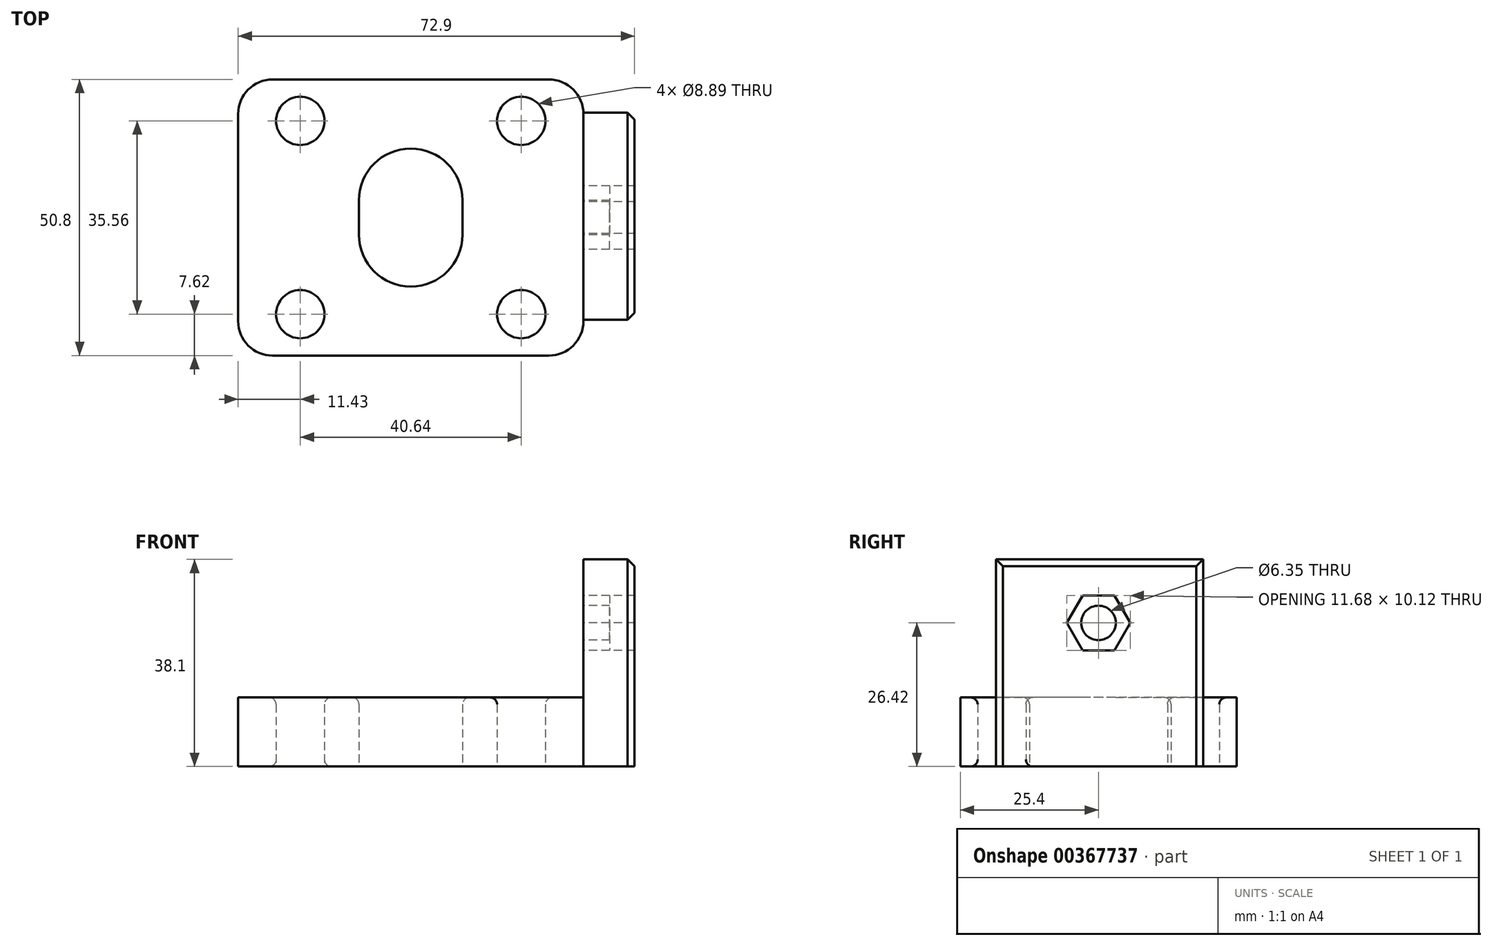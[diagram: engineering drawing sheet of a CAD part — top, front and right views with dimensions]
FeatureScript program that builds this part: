
annotation { "Feature Type Name" : "Feature", "Feature Type Description" : "" }
export const myFeature = defineFeature(function(context is Context, id is Id, definition is map)
    precondition{}
    {
        {
            var Q0;
            Q0=qCreatedBy(makeId("Top.planeOp"),FACE);
            var sketch = newSketch(context, id + "F0", { "sketchPlane" : qUnion([Q0])});
            skLineSegment(sketch, "E0.bottom", {"start": v(25.4, 25.4) * mm, "end": v(-25.4, 25.4) * mm});
            skLineSegment(sketch, "E0.top", {"start": v(25.4, -25.4) * mm, "end": v(-25.4, -25.4) * mm});
            skLineSegment(sketch, "E0.left", {"start": v(31.75, 19.05) * mm, "end": v(31.75, -19.05) * mm});
            skLineSegment(sketch, "E0.right", {"start": v(-31.75, 19.05) * mm, "end": v(-31.75, -19.05) * mm});
            skPoint(sketch, "E0.middle", {"position": v(0, 0) * mm});
            skCircle(sketch, "E1", {"center": v(-20.32, 17.78) * mm, "radius": 4.45 * mm});
            skCircle(sketch, "E2.MirrorC", {"center": v(20.32, 17.78) * mm, "radius": 4.45 * mm});
            skCircle(sketch, "E3.MirrorC", {"center": v(20.32, -17.78) * mm, "radius": 4.45 * mm});
            skCircle(sketch, "E4.MirrorC", {"center": v(-20.32, -17.78) * mm, "radius": 4.45 * mm});
            skPoint(sketch, "E5.visualSharp", {"position": v(-31.75, 25.4) * mm});
            skArc(sketch, "E5.filletArc", {"start": v(-25.4, 25.4) * mm, "mid": v(-29.9, 23.54) * mm, "end": v(-31.75, 19.05) * mm});
            skPoint(sketch, "E6.visualSharp", {"position": v(31.75, 25.4) * mm});
            skArc(sketch, "E6.filletArc", {"start": v(31.75, 19.05) * mm, "mid": v(29.9, 23.54) * mm, "end": v(25.4, 25.4) * mm});
            skPoint(sketch, "E7.visualSharp", {"position": v(31.75, -25.4) * mm});
            skArc(sketch, "E7.filletArc", {"start": v(25.4, -25.4) * mm, "mid": v(29.9, -23.54) * mm, "end": v(31.75, -19.05) * mm});
            skPoint(sketch, "E8.visualSharp", {"position": v(-31.75, -25.4) * mm});
            skArc(sketch, "E8.filletArc", {"start": v(-31.75, -19.05) * mm, "mid": v(-29.9, -23.54) * mm, "end": v(-25.4, -25.4) * mm});
            skLineSegment(sketch, "E9.bottom", {"start": v(0, 12.7) * mm, "end": v(0, 12.7) * mm});
            skLineSegment(sketch, "E9.top", {"start": v(0, -12.7) * mm, "end": v(0, -12.7) * mm});
            skLineSegment(sketch, "E9.left", {"start": v(9.53, 3.18) * mm, "end": v(9.53, -3.17) * mm});
            skLineSegment(sketch, "E9.right", {"start": v(-9.53, 3.18) * mm, "end": v(-9.53, -3.18) * mm});
            skPoint(sketch, "E10.visualSharp", {"position": v(-9.53, 12.7) * mm});
            skArc(sketch, "E10.filletArc", {"start": v(0, 12.7) * mm, "mid": v(-6.74, 9.91) * mm, "end": v(-9.53, 3.17) * mm});
            skPoint(sketch, "E11.visualSharp", {"position": v(-9.53, -12.7) * mm});
            skArc(sketch, "E11.filletArc", {"start": v(-9.53, -3.18) * mm, "mid": v(-6.74, -9.91) * mm, "end": v(0, -12.7) * mm});
            skPoint(sketch, "E12.visualSharp", {"position": v(9.53, -12.7) * mm});
            skArc(sketch, "E12.filletArc", {"start": v(0, -12.7) * mm, "mid": v(6.74, -9.91) * mm, "end": v(9.53, -3.18) * mm});
            skPoint(sketch, "E13.visualSharp", {"position": v(9.53, 12.7) * mm});
            skArc(sketch, "E13.filletArc", {"start": v(9.53, 3.18) * mm, "mid": v(6.74, 9.91) * mm, "end": v(0, 12.7) * mm});
            skSolve(sketch);
        }
        {
            var Q0;
            Q0=makeQuery(id+"F0.imprint","IMPRINT",FACE,{"disambiguationData":[TD([[makeQuery(id+"F0.imprint","IMPRINT",EDGE,{"derivedFrom":sQuery(id+"F0.wireOp",EDGE,"E0.bottom")}),1.0]])]});
            extrude(context, id + "F1", {"entities" : qUnion([Q0]), "depth" : 12.7 * mm});
        }
        {
            var Q0;
            Q0=makeQuery(id+"F1.opExtrude","CAP_EDGE",EDGE,{"disambiguationData":[OSD([sQuery(id+"F0.wireOp",EDGE,"E1")])],"isStart":false});
            var Q1;
            Q1=makeQuery(id+"F1.opExtrude","SWEPT_FACE",FACE,{"disambiguationData":[OSD([sQuery(id+"F0.wireOp",EDGE,"E4.MirrorC")])]});
            var Q2;
            Q2=makeQuery(id+"F1.opExtrude","CAP_EDGE",EDGE,{"disambiguationData":[OSD([sQuery(id+"F0.wireOp",EDGE,"E3.MirrorC")])],"isStart":false});
            var Q3;
            Q3=makeQuery(id+"F1.opExtrude","CAP_EDGE",EDGE,{"disambiguationData":[OSD([sQuery(id+"F0.wireOp",EDGE,"E2.MirrorC")])],"isStart":false});
            var Q4;
            Q4=makeQuery(id+"F1.opExtrude","CAP_EDGE",EDGE,{"disambiguationData":[OSD([sQuery(id+"F0.wireOp",EDGE,"E11.filletArc"),sQuery(id+"F0.wireOp",EDGE,"E12.filletArc")])],"isStart":false});
            var Q5;
            Q5=makeQuery(id+"F1.opExtrude","CAP_EDGE",EDGE,{"disambiguationData":[OSD([sQuery(id+"F0.wireOp",EDGE,"E9.right")])],"isStart":false});
            var Q6;
            Q6=makeQuery(id+"F1.opExtrude","CAP_EDGE",EDGE,{"disambiguationData":[OSD([sQuery(id+"F0.wireOp",EDGE,"E10.filletArc"),sQuery(id+"F0.wireOp",EDGE,"E13.filletArc")])],"isStart":false});
            var Q7;
            Q7=makeQuery(id+"F1.opExtrude","CAP_EDGE",EDGE,{"disambiguationData":[OSD([sQuery(id+"F0.wireOp",EDGE,"E9.left")])],"isStart":false});
            fillet(context, id + "F2", {"entities" : qUnion([Q0, Q1, Q2, Q3, Q4, Q5, Q6, Q7]), "radius" : 1.27 * mm, "tangentPropagation" : true, "allowEdgeOverflow" : false});
        }
        {
            var Q0;
            Q0=qCreatedBy(makeId("Right.planeOp"),FACE);
            var sketch = newSketch(context, id + "F3", { "sketchPlane" : qUnion([Q0])});
            skLineSegment(sketch, "E14.bottom", {"start": v(-18.83, 0) * mm, "end": v(19.27, 0) * mm});
            skLineSegment(sketch, "E14.top", {"start": v(-18.83, 38.1) * mm, "end": v(19.27, 38.1) * mm});
            skLineSegment(sketch, "E14.left", {"start": v(-18.83, 0) * mm, "end": v(-18.83, 38.1) * mm});
            skLineSegment(sketch, "E14.right", {"start": v(19.27, 0) * mm, "end": v(19.27, 38.1) * mm});
            skCircle(sketch, "E15.cCircle", {"center": v(0, 26.42) * mm, "radius": 5.06 * mm, "construction": true});
            skLineSegment(sketch, "E15.0", {"start": v(2.92, 21.36) * mm, "end": v(-2.92, 21.36) * mm});
            skLineSegment(sketch, "E15.1", {"start": v(-2.92, 21.36) * mm, "end": v(-5.84, 26.42) * mm});
            skLineSegment(sketch, "E15.2", {"start": v(-5.84, 26.42) * mm, "end": v(-2.92, 31.48) * mm});
            skLineSegment(sketch, "E15.3", {"start": v(-2.92, 31.48) * mm, "end": v(2.92, 31.48) * mm});
            skLineSegment(sketch, "E15.4", {"start": v(2.92, 31.48) * mm, "end": v(5.84, 26.42) * mm});
            skLineSegment(sketch, "E15.5", {"start": v(5.84, 26.42) * mm, "end": v(2.92, 21.36) * mm});
            skPoint(sketch, "E15.0.midPoint", {"position": v(0, 21.36) * mm});
            skCircle(sketch, "E16", {"center": v(0, 26.42) * mm, "radius": 3.18 * mm});
            skSolve(sketch);
        }
        {
            var Q0;
            Q0=makeQuery(id+"F3.imprint","IMPRINT",FACE,{"disambiguationData":[TD([[makeQuery(id+"F3.imprint","IMPRINT",EDGE,{"derivedFrom":sQuery(id+"F3.wireOp",EDGE,"E15.0")}),-1.0]])]});
            extrude(context, id + "F4", {"entities" : qUnion([Q0]), "depth" : 36.58 * mm, "hasSecondDirection" : true, "secondDirectionOppositeDirection" : false, "secondDirectionDepth" : 31.75 * mm});
        }
        {
            var Q0;
            Q0 = qSketchRegion(id + "F3", true);
            extrude(context, id + "F5", {"entities" : qUnion([Q0]), "depth" : 41.15 * mm, "hasSecondDirection" : true, "secondDirectionOppositeDirection" : false, "secondDirectionDepth" : 31.75 * mm});
        }
        {
            var Q0;
            Q0=makeQuery(id+"F5.opExtrude","CAP_EDGE",EDGE,{"disambiguationData":[OSD([sQuery(id+"F3.wireOp",EDGE,"E14.top")])],"isStart":false});
            var Q1;
            Q1=makeQuery(id+"F5.opExtrude","CAP_EDGE",EDGE,{"disambiguationData":[OSD([sQuery(id+"F3.wireOp",EDGE,"E14.left")])],"isStart":false});
            var Q2;
            Q2=makeQuery(id+"F5.opExtrude","CAP_EDGE",EDGE,{"disambiguationData":[OSD([sQuery(id+"F3.wireOp",EDGE,"E14.right")])],"isStart":false});
            chamfer(context, id + "F6", {"entities" : qUnion([Q0, Q1, Q2]), "width" : 1.27 * mm, "tangentPropagation" : true});
        }
    });
